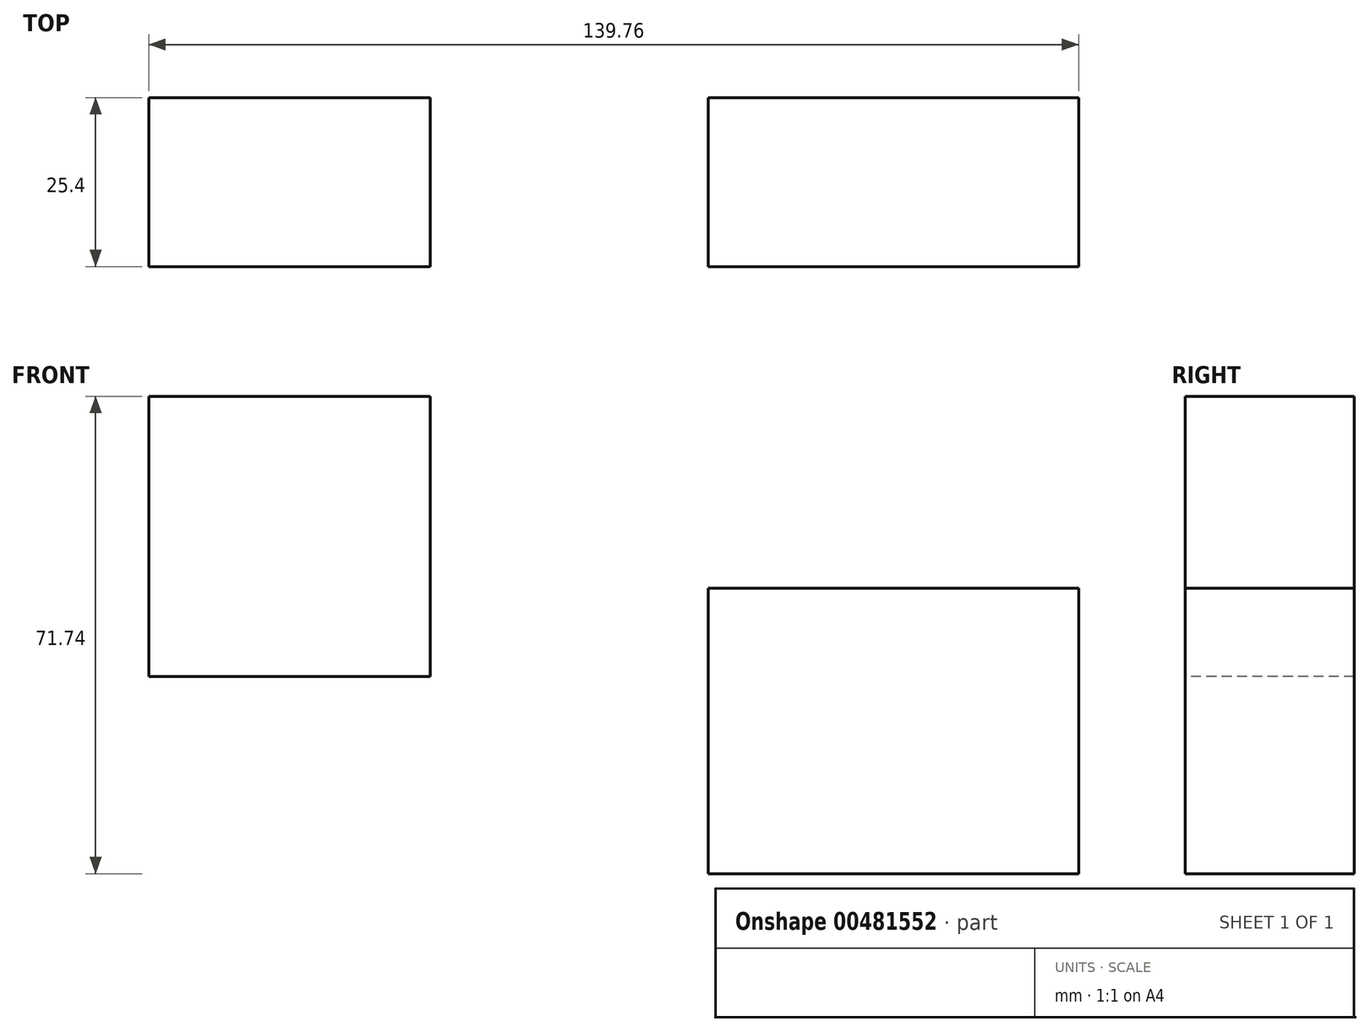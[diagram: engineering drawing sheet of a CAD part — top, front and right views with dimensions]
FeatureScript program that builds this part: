
annotation { "Feature Type Name" : "Feature", "Feature Type Description" : "" }
export const myFeature = defineFeature(function(context is Context, id is Id, definition is map)
    precondition{}
    {
        {
            var Q0;
            Q0=qCreatedBy(makeId("Front.planeOp"),FACE);
            var sketch = newSketch(context, id + "F0", { "sketchPlane" : qUnion([Q0])});
            skLineSegment(sketch, "E0.bottom", {"start": v(-80.58, 35.01) * mm, "end": v(-38.3, 35.01) * mm});
            skLineSegment(sketch, "E0.top", {"start": v(-80.58, 77.13) * mm, "end": v(-38.3, 77.13) * mm});
            skLineSegment(sketch, "E0.left", {"start": v(-80.58, 35.01) * mm, "end": v(-80.58, 77.13) * mm});
            skLineSegment(sketch, "E0.right", {"start": v(-38.3, 35.01) * mm, "end": v(-38.3, 77.13) * mm});
            skPoint(sketch, "E0.middle", {"position": v(-59.44, 56.07) * mm});
            skLineSegment(sketch, "E1.bottom", {"start": v(3.48, 5.39) * mm, "end": v(59.18, 5.39) * mm});
            skLineSegment(sketch, "E1.top", {"start": v(3.48, 48.28) * mm, "end": v(59.18, 48.28) * mm});
            skLineSegment(sketch, "E1.left", {"start": v(3.48, 5.39) * mm, "end": v(3.48, 48.28) * mm});
            skLineSegment(sketch, "E1.right", {"start": v(59.18, 5.39) * mm, "end": v(59.18, 48.28) * mm});
            skPoint(sketch, "E1.middle", {"position": v(31.33, 26.83) * mm});
            skSolve(sketch);
        }
        {
            var Q0;
            Q0=makeQuery(id+"F0.imprint","IMPRINT",FACE,{"disambiguationData":[TD([[makeQuery(id+"F0.imprint","IMPRINT",EDGE,{"derivedFrom":sQuery(id+"F0.wireOp",EDGE,"E0.bottom")}),1.0]])]});
            var Q1;
            Q1=makeQuery(id+"F0.imprint","IMPRINT",FACE,{"disambiguationData":[TD([[makeQuery(id+"F0.imprint","IMPRINT",EDGE,{"derivedFrom":sQuery(id+"F0.wireOp",EDGE,"E1.bottom")}),1.0]])]});
            var Q2;
            Q2=sQuery(id+"F0.wireOp",EDGE,"E0.bottom");
            var Q3;
            Q3=sQuery(id+"F0.wireOp",EDGE,"E0.top");
            var Q4;
            Q4=sQuery(id+"F0.wireOp",EDGE,"E0.left");
            var Q5;
            Q5=sQuery(id+"F0.wireOp",EDGE,"E0.right");
            var Q6;
            Q6=sQuery(id+"F0.wireOp",EDGE,"E1.bottom");
            var Q7;
            Q7=sQuery(id+"F0.wireOp",EDGE,"E1.top");
            var Q8;
            Q8=sQuery(id+"F0.wireOp",EDGE,"E1.left");
            var Q9;
            Q9=sQuery(id+"F0.wireOp",EDGE,"E1.right");
            extrude(context, id + "F1", {"entities" : qUnion([Q0, Q1]), "bodyType" : ToolBodyType.SURFACE, "surfaceEntities" : qUnion([Q2, Q3, Q4, Q5, Q6, Q7, Q8, Q9]), "depth" : 25.4 * mm});
        }
    });
